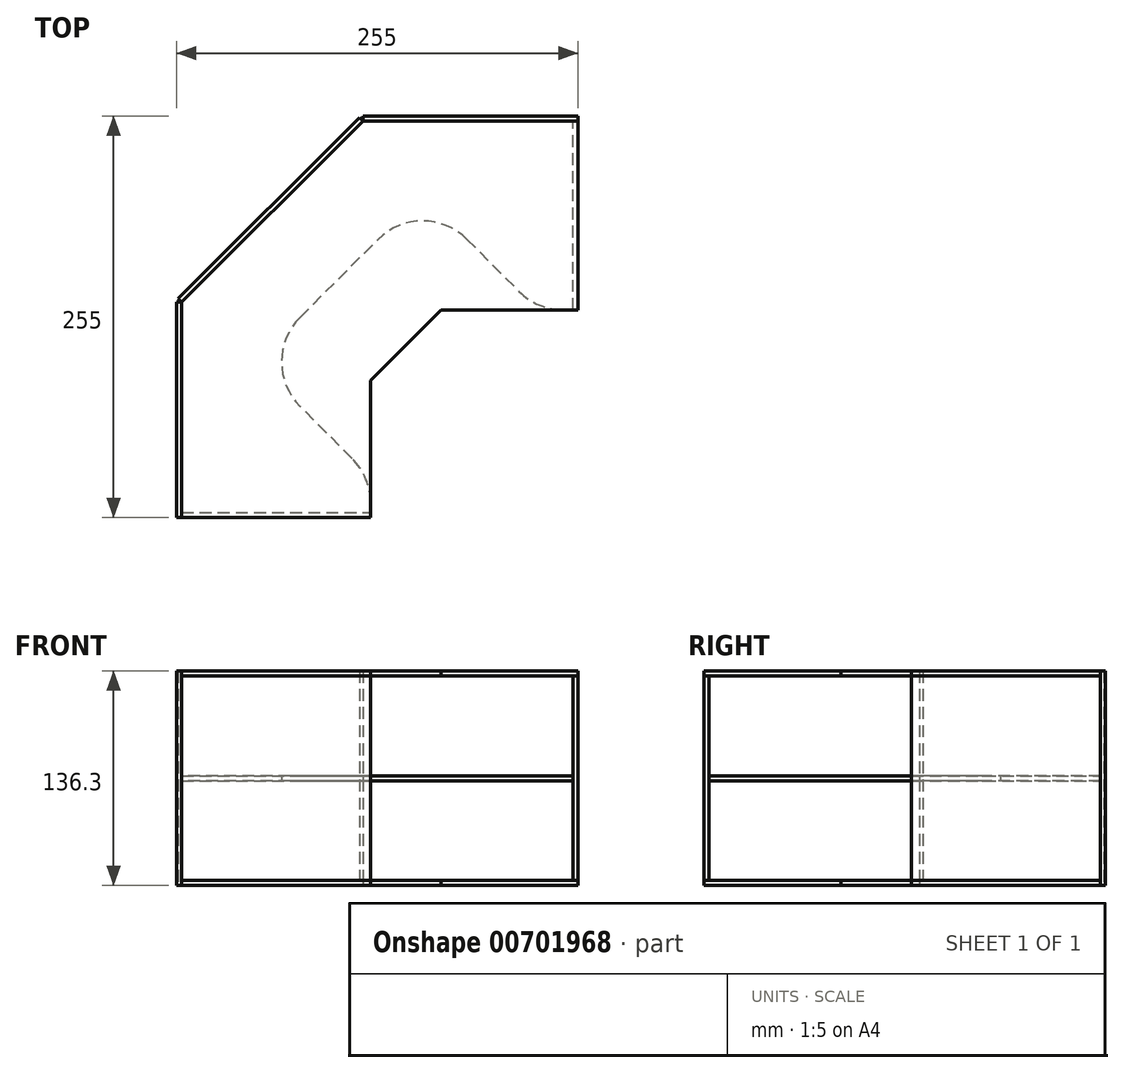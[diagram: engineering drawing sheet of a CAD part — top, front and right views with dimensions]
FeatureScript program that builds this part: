
annotation { "Feature Type Name" : "Feature", "Feature Type Description" : "" }
export const myFeature = defineFeature(function(context is Context, id is Id, definition is map)
    precondition{}
    {
        {
            assignVariable(context, id + "F0", {"name" : "x", "anyValue" : 3.15});
        }
        {
            var Q0;
            Q0=qCreatedBy(makeId("Top.planeOp"),FACE);
            var sketch = newSketch(context, id + "F1", { "sketchPlane" : qUnion([Q0])});
            skLineSegment(sketch, "E0", {"start": v(0, 0) * mm, "end": v(120, 0) * mm});
            skLineSegment(sketch, "E1", {"start": v(120, 0) * mm, "end": v(120, 87) * mm});
            skLineSegment(sketch, "E2", {"start": v(120, 87) * mm, "end": v(164.85, 131.85) * mm});
            skLineSegment(sketch, "E3", {"start": v(164.85, 131.85) * mm, "end": v(251.85, 131.85) * mm});
            skLineSegment(sketch, "E4", {"start": v(251.85, 131.85) * mm, "end": v(251.85, 251.85) * mm});
            skLineSegment(sketch, "E5", {"start": v(251.85, 251.85) * mm, "end": v(115.14, 251.85) * mm});
            skLineSegment(sketch, "E6", {"start": v(115.14, 251.85) * mm, "end": v(0, 136.7) * mm});
            skLineSegment(sketch, "E7", {"start": v(0, 136.7) * mm, "end": v(0, 0) * mm});
            skLineSegment(sketch, "E8", {"start": v(0, 136.7) * mm, "end": v(0, 251.85) * mm, "construction": true});
            skLineSegment(sketch, "E9", {"start": v(0, 251.85) * mm, "end": v(115.14, 251.85) * mm, "construction": true});
            skLineSegment(sketch, "E10", {"start": v(251.85, 131.85) * mm, "end": v(251.85, 0) * mm, "construction": true});
            skLineSegment(sketch, "E11", {"start": v(251.85, 0) * mm, "end": v(120, 0) * mm, "construction": true});
            skLineSegment(sketch, "E12", {"start": v(251.85, 0) * mm, "end": v(142.42, 109.42) * mm, "construction": true});
            skLineSegment(sketch, "E13", {"start": v(142.43, 109.42) * mm, "end": v(57.57, 194.28) * mm, "construction": true});
            skLineSegment(sketch, "E14", {"start": v(57.57, 194.28) * mm, "end": v(0, 251.85) * mm, "construction": true});
            skLineSegment(sketch, "E15.0", {"start": v(-3.15, 104.14) * mm, "end": v(-3.15, 0) * mm});
            skSolve(sketch);
        }
        {
            var Q0;
            Q0=qSketchRegion(id+"F1",true);
            extrude(context, id + "F2", {"entities" : qUnion([Q0]), "depth" : (getVariable(context, 'x')) * mm, "offsetDistance" : 25 * mm});
        }
        {
            var Q0;
            Q0=makeQuery(id+"F2.opExtrude","SWEPT_FACE",FACE,{"disambiguationData":[OSD([sQuery(id+"F1.wireOp",EDGE,"E0")])]});
            var sketch = newSketch(context, id + "F3", { "sketchPlane" : qUnion([Q0])});
            skLineSegment(sketch, "E16.bottom", {"start": v(0, 0) * mm, "end": v(120, 0) * mm});
            skLineSegment(sketch, "E16.top", {"start": v(0, -130) * mm, "end": v(120, -130) * mm});
            skLineSegment(sketch, "E16.left", {"start": v(0, 0) * mm, "end": v(0, -130) * mm});
            skLineSegment(sketch, "E16.right", {"start": v(120, 0) * mm, "end": v(120, -130) * mm});
            skSolve(sketch);
        }
        {
            var Q0;
            Q0=qSketchRegion(id+"F3",true);
            extrude(context, id + "F4", {"entities" : qUnion([Q0]), "oppositeDirection" : true, "depth" : (getVariable(context, 'x')) * mm, "offsetDistance" : 25 * mm});
        }
        {
            var Q0;
            Q0=makeQuery(id+"F2.opExtrude","SWEPT_FACE",FACE,{"disambiguationData":[OSD([sQuery(id+"F1.wireOp",EDGE,"E4")])]});
            var sketch = newSketch(context, id + "F5", { "sketchPlane" : qUnion([Q0])});
            skLineSegment(sketch, "E17.bottom", {"start": v(131.85, 0) * mm, "end": v(251.85, 0) * mm});
            skLineSegment(sketch, "E17.top", {"start": v(131.85, -130) * mm, "end": v(251.85, -130) * mm});
            skLineSegment(sketch, "E17.left", {"start": v(131.85, 0) * mm, "end": v(131.85, -130) * mm});
            skLineSegment(sketch, "E17.right", {"start": v(251.85, 0) * mm, "end": v(251.85, -130) * mm});
            skSolve(sketch);
        }
        {
            var Q0;
            Q0=qSketchRegion(id+"F5",true);
            extrude(context, id + "F6", {"entities" : qUnion([Q0]), "oppositeDirection" : true, "depth" : (getVariable(context, 'x')) * mm, "offsetDistance" : 25 * mm});
        }
        {
            var Q0;
            Q0=makeQuery(id+"F2.opExtrude","SWEPT_BODY",BODY,{"disambiguationData":[OSD([sQuery(id+"F1.wireOp",EDGE,"E0"),sQuery(id+"F1.wireOp",EDGE,"E1"),sQuery(id+"F1.wireOp",EDGE,"E2"),sQuery(id+"F1.wireOp",EDGE,"E3"),sQuery(id+"F1.wireOp",EDGE,"E4"),sQuery(id+"F1.wireOp",EDGE,"E5"),sQuery(id+"F1.wireOp",EDGE,"E6"),sQuery(id+"F1.wireOp",EDGE,"E7")])]});
            transform(context, id + "F7", {"entities" : qUnion([Q0]), "transformType" : TransformType.TRANSLATION_3D, "dx" : 0 * mm, "dy" : 0 * mm, "dz" : (-130 - 3.15) * mm, "makeCopy" : true});
        }
        {
            var Q0;
            Q0=makeQuery(id+"F2.opExtrude","SWEPT_FACE",FACE,{"disambiguationData":[OSD([sQuery(id+"F1.wireOp",EDGE,"E7")])]});
            var sketch = newSketch(context, id + "F8", { "sketchPlane" : qUnion([Q0])});
            skLineSegment(sketch, "E18.bottom", {"start": v(0, 3.15) * mm, "end": v(-136.7, 3.15) * mm});
            skLineSegment(sketch, "E18.top", {"start": v(0, -133.15) * mm, "end": v(-136.7, -133.15) * mm});
            skLineSegment(sketch, "E18.left", {"start": v(0, 3.15) * mm, "end": v(0, -133.15) * mm});
            skLineSegment(sketch, "E18.right", {"start": v(-136.7, 3.15) * mm, "end": v(-136.7, -133.15) * mm});
            skSolve(sketch);
        }
        {
            var Q0;
            Q0=qSketchRegion(id+"F8",true);
            extrude(context, id + "F9", {"entities" : qUnion([Q0]), "depth" : (getVariable(context, 'x')) * mm, "offsetDistance" : 25 * mm});
        }
        {
            var Q0;
            Q0=makeQuery(id+"F2.opExtrude","SWEPT_FACE",FACE,{"disambiguationData":[OSD([sQuery(id+"F1.wireOp",EDGE,"E5")])]});
            var sketch = newSketch(context, id + "F10", { "sketchPlane" : qUnion([Q0])});
            skLineSegment(sketch, "E19.bottom", {"start": v(-251.85, 3.15) * mm, "end": v(-115.14, 3.15) * mm});
            skLineSegment(sketch, "E19.top", {"start": v(-251.85, -133.15) * mm, "end": v(-115.14, -133.15) * mm});
            skLineSegment(sketch, "E19.left", {"start": v(-251.85, 3.15) * mm, "end": v(-251.85, -133.15) * mm});
            skLineSegment(sketch, "E19.right", {"start": v(-115.14, 3.15) * mm, "end": v(-115.14, -133.15) * mm});
            skSolve(sketch);
        }
        {
            var Q0;
            Q0=qSketchRegion(id+"F10",true);
            extrude(context, id + "F11", {"entities" : qUnion([Q0]), "depth" : (getVariable(context, 'x')) * mm, "offsetDistance" : 25 * mm});
        }
        {
            var Q0;
            Q0=makeQuery(id+"F7.opPattern","COPY",FACE,{"derivedFrom":makeQuery(id+"F2.opExtrude","SWEPT_FACE",FACE,{"disambiguationData":[OSD([sQuery(id+"F1.wireOp",EDGE,"E6")])]}),"instanceName":"1"});
            var sketch = newSketch(context, id + "F12", { "sketchPlane" : qUnion([Q0])});
            skLineSegment(sketch, "E20.bottom", {"start": v(-259.5, 3.15) * mm, "end": v(-96.67, 3.15) * mm});
            skLineSegment(sketch, "E20.top", {"start": v(-259.5, -133.15) * mm, "end": v(-96.67, -133.15) * mm});
            skLineSegment(sketch, "E20.left", {"start": v(-259.5, 3.15) * mm, "end": v(-259.5, -133.15) * mm});
            skLineSegment(sketch, "E20.right", {"start": v(-96.67, 3.15) * mm, "end": v(-96.67, -133.15) * mm});
            skSolve(sketch);
        }
        {
            var Q0;
            Q0=qSketchRegion(id+"F12",true);
            extrude(context, id + "F13", {"entities" : qUnion([Q0]), "depth" : (getVariable(context, 'x')) * mm, "offsetDistance" : 25 * mm});
        }
        {
            var Q0;
            Q0=makeQuery(id+"F7.opPattern","COPY",FACE,{"derivedFrom":makeQuery(id+"F2.opExtrude","CAP_FACE",FACE,{"disambiguationData":[OSD([sQuery(id+"F1.wireOp",EDGE,"E0"),sQuery(id+"F1.wireOp",EDGE,"E1"),sQuery(id+"F1.wireOp",EDGE,"E2"),sQuery(id+"F1.wireOp",EDGE,"E3"),sQuery(id+"F1.wireOp",EDGE,"E4"),sQuery(id+"F1.wireOp",EDGE,"E5"),sQuery(id+"F1.wireOp",EDGE,"E6"),sQuery(id+"F1.wireOp",EDGE,"E7")])],"isStart":false}),"instanceName":"1"});
            cPlane(context, id + "F14", {"entities" : qUnion([Q0]), "cplaneType" : CPlaneType.OFFSET, "offset" : 63.42 * mm, "width" : 150 * mm, "height" : 150 * mm});
        }
        {
            var Q0;
            Q0=qCreatedBy(id+"F14.planeOp",FACE);
            var sketch = newSketch(context, id + "F15", { "sketchPlane" : qUnion([Q0])});
            skLineSegment(sketch, "E21.0", {"start": v(248.7, 251.85) * mm, "end": v(115.14, 251.85) * mm});
            skLineSegment(sketch, "E21.1", {"start": v(248.7, 131.85) * mm, "end": v(248.7, 251.85) * mm});
            skLineSegment(sketch, "E21.2", {"start": v(115.14, 251.85) * mm, "end": v(0, 136.7) * mm});
            skLineSegment(sketch, "E21.3", {"start": v(242.63, 131.85) * mm, "end": v(248.7, 131.85) * mm});
            skLineSegment(sketch, "E21.4", {"start": v(0, 136.7) * mm, "end": v(0, 3.15) * mm});
            skLineSegment(sketch, "E21.5", {"start": v(0, 3.15) * mm, "end": v(120, 3.15) * mm});
            skLineSegment(sketch, "E21.6", {"start": v(120, 3.15) * mm, "end": v(120, 9.22) * mm});
            skLineSegment(sketch, "E22", {"start": v(75.25, 127.1) * mm, "end": v(124.75, 176.6) * mm});
            skLineSegment(sketch, "E23", {"start": v(181.32, 176.6) * mm, "end": v(214.35, 143.57) * mm});
            skLineSegment(sketch, "E24", {"start": v(108.28, 37.5) * mm, "end": v(75.25, 70.53) * mm});
            skPoint(sketch, "E25", {"position": v(100, 151.85) * mm});
            skPoint(sketch, "E26.visualSharp", {"position": v(46.97, 98.82) * mm});
            skArc(sketch, "E26.filletArc", {"start": v(75.25, 127.1) * mm, "mid": v(63.53, 98.82) * mm, "end": v(75.25, 70.53) * mm});
            skPoint(sketch, "E27.visualSharp", {"position": v(153.03, 204.88) * mm});
            skArc(sketch, "E27.filletArc", {"start": v(181.32, 176.6) * mm, "mid": v(153.03, 188.32) * mm, "end": v(124.75, 176.6) * mm});
            skArc(sketch, "E28.filletArc", {"start": v(120, 9.22) * mm, "mid": v(116.96, 24.52) * mm, "end": v(108.28, 37.5) * mm});
            skArc(sketch, "E29.filletArc", {"start": v(214.35, 143.57) * mm, "mid": v(227.33, 134.9) * mm, "end": v(242.63, 131.85) * mm});
            skLineSegment(sketch, "E30", {"start": v(100, 151.85) * mm, "end": v(142.42, 109.42) * mm, "construction": true});
            skSolve(sketch);
        }
        {
            var Q0;
            Q0 = qSketchRegion(id + "F15", true);
            extrude(context, id + "F16", {"entities" : qUnion([Q0]), "depth" : (getVariable(context, 'x')) * mm, "offsetDistance" : 25 * mm});
        }
    });
